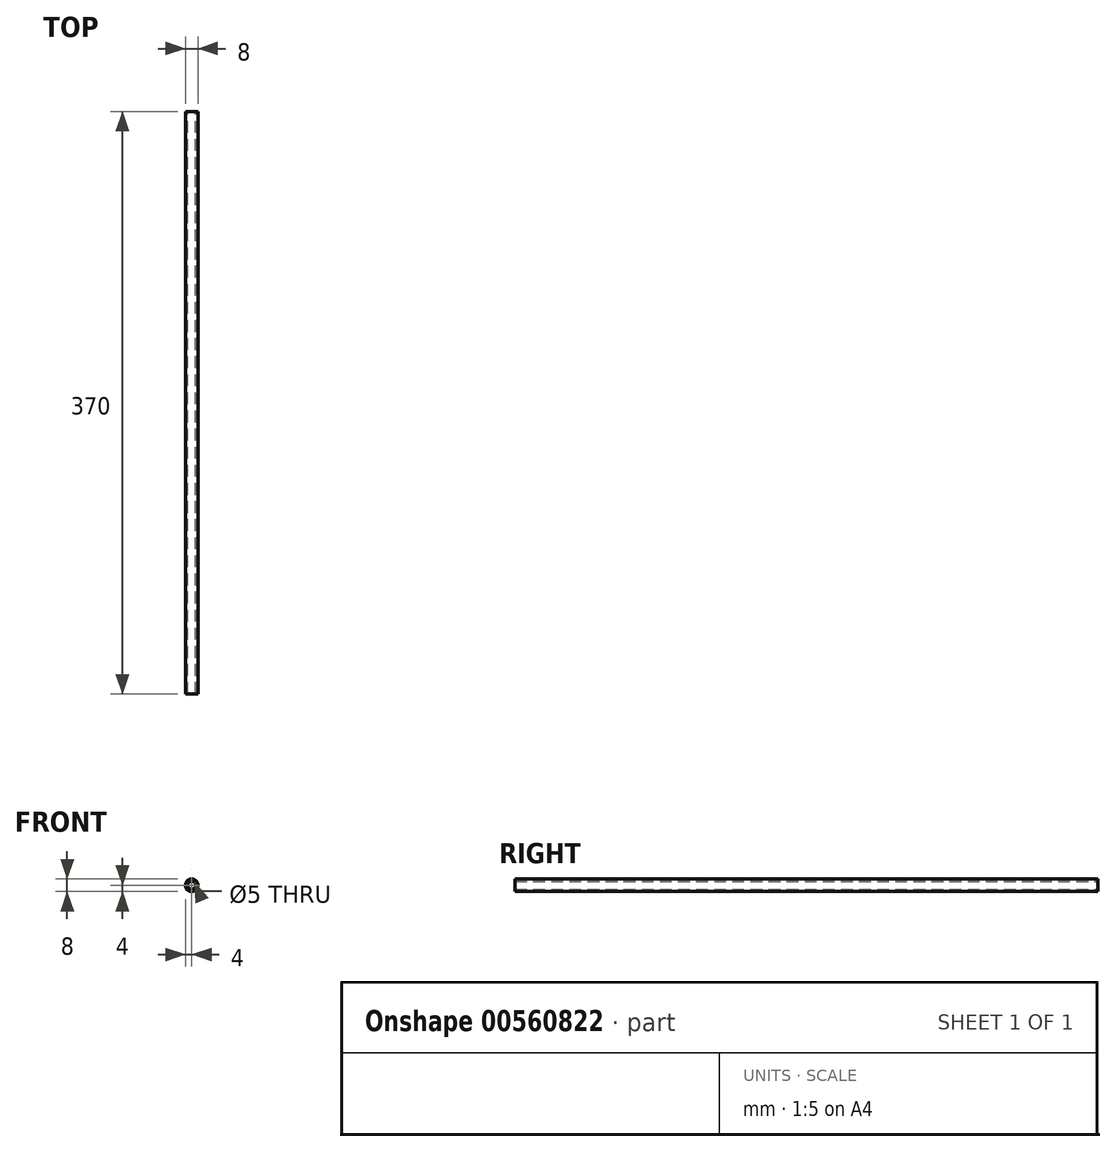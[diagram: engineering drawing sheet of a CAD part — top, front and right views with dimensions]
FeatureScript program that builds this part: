
annotation { "Feature Type Name" : "Feature", "Feature Type Description" : "" }
export const myFeature = defineFeature(function(context is Context, id is Id, definition is map)
    precondition{}
    {
        {
            var Q0;
            Q0=qCreatedBy(makeId("Front.planeOp"),FACE);
            var sketch = newSketch(context, id + "F0", { "sketchPlane" : qUnion([Q0])});
            skCircle(sketch, "E0", {"center": v(0, 0) * mm, "radius": 4 * mm});
            skCircle(sketch, "E1", {"center": v(0, 0) * mm, "radius": 2.5 * mm});
            skSolve(sketch);
        }
        {
            var Q0;
            Q0=qSketchRegion(id+"F0",true);
            extrude(context, id + "F1", {"entities" : qUnion([Q0]), "endBound" : BoundingType.SYMMETRIC, "depth" : 370 * mm, "offsetDistance" : 25 * mm});
        }
    });
